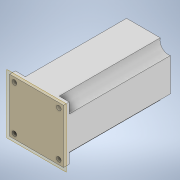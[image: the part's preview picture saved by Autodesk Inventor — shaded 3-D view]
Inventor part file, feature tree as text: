
AUTODESK INVENTOR PART (.ipt)
format: ipt  version: 2020 (Build 240168000, 168)  size: 128,512 bytes
history: native  units: mm
features: extrude x2, sketch x2
ambient origin geometry x8: Origin, YZ Plane, XZ Plane, XY Plane, X Axis, Y Axis, Z Axis, Center Point
bodies: Solid1 (feature_tree)
feature tree (4):
  extrude  "Extrusion1"  Depth=57.0mm
  extrude  "Extrusion2"  Depth=107.0mm
  sketch  "Sketch1"  dims[d0=57.0mm d1=57.0mm]
  sketch  "Sketch2"  dims[d2=5.0mm d3=5.0mm d4=5.0mm d5=113.0mm d6=0.0mm d7=107.0mm d8=0.0mm]
